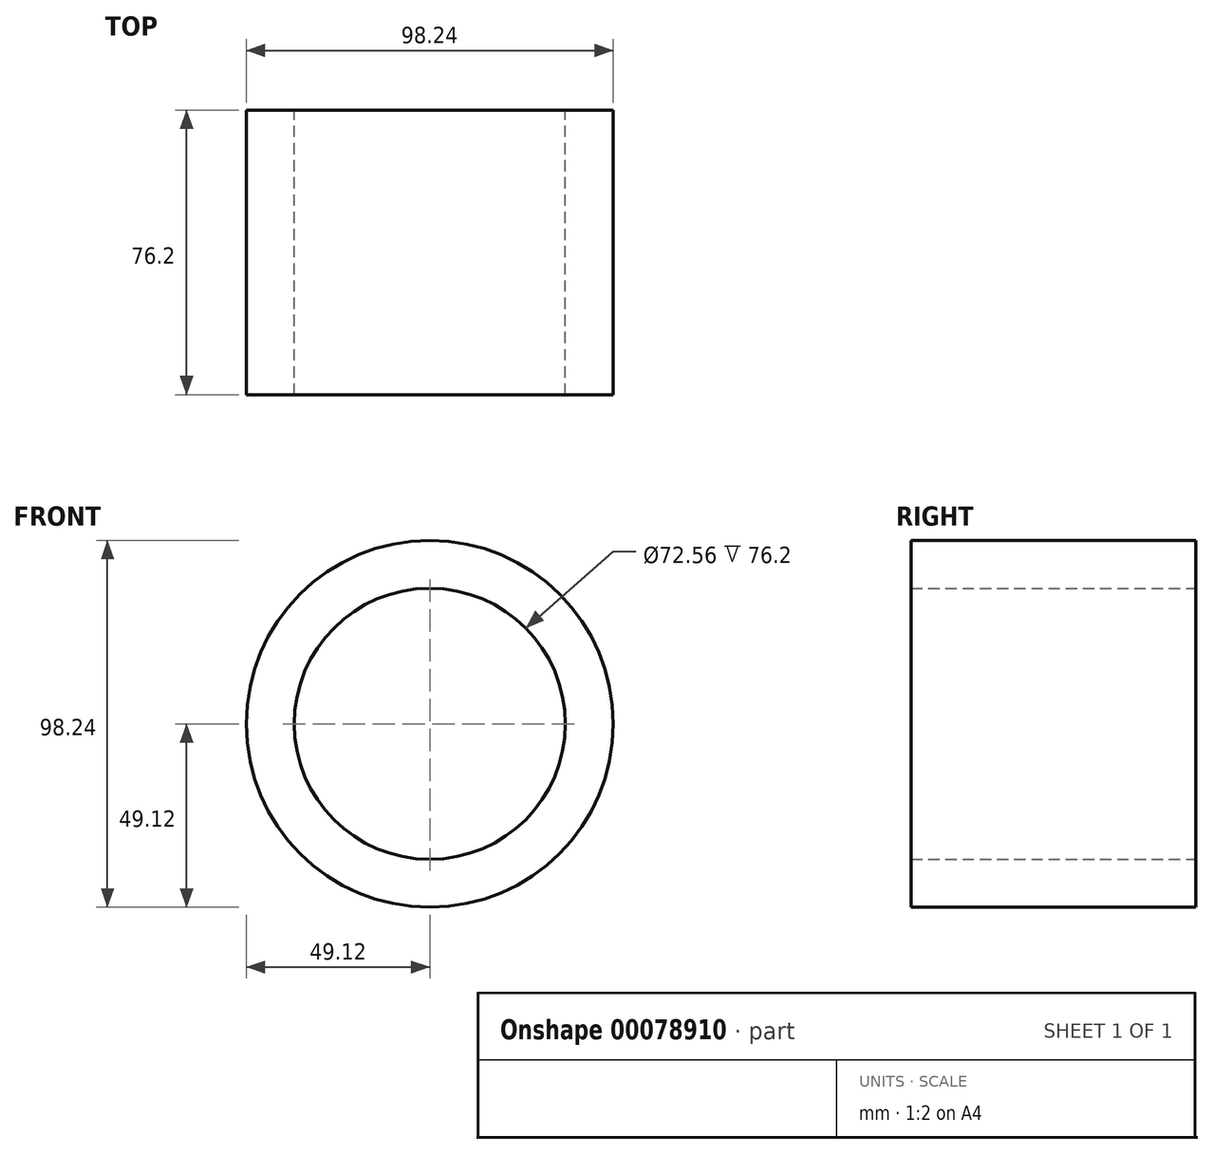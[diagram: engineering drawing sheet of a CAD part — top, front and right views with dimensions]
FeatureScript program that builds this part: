
annotation { "Feature Type Name" : "Feature", "Feature Type Description" : "" }
export const myFeature = defineFeature(function(context is Context, id is Id, definition is map)
    precondition{}
    {
        {
            var Q0;
            Q0=qCreatedBy(makeId("Front.planeOp"),FACE);
            var sketch = newSketch(context, id + "F0", { "sketchPlane" : qUnion([Q0])});
            skCircle(sketch, "E0", {"center": v(0, 0) * mm, "radius": 49.12 * mm});
            skCircle(sketch, "E1", {"center": v(0, 0) * mm, "radius": 36.28 * mm});
            skSolve(sketch);
        }
        {
            var Q0;
            Q0=makeQuery(id+"F0.imprint","IMPRINT",FACE,{"disambiguationData":[TD([[makeQuery(id+"F0.imprint","IMPRINT",EDGE,{"derivedFrom":sQuery(id+"F0.wireOp",EDGE,"E0")}),1.0]])]});
            extrude(context, id + "F1", {"entities" : qUnion([Q0]), "depth" : 76.2 * mm});
        }
    });
